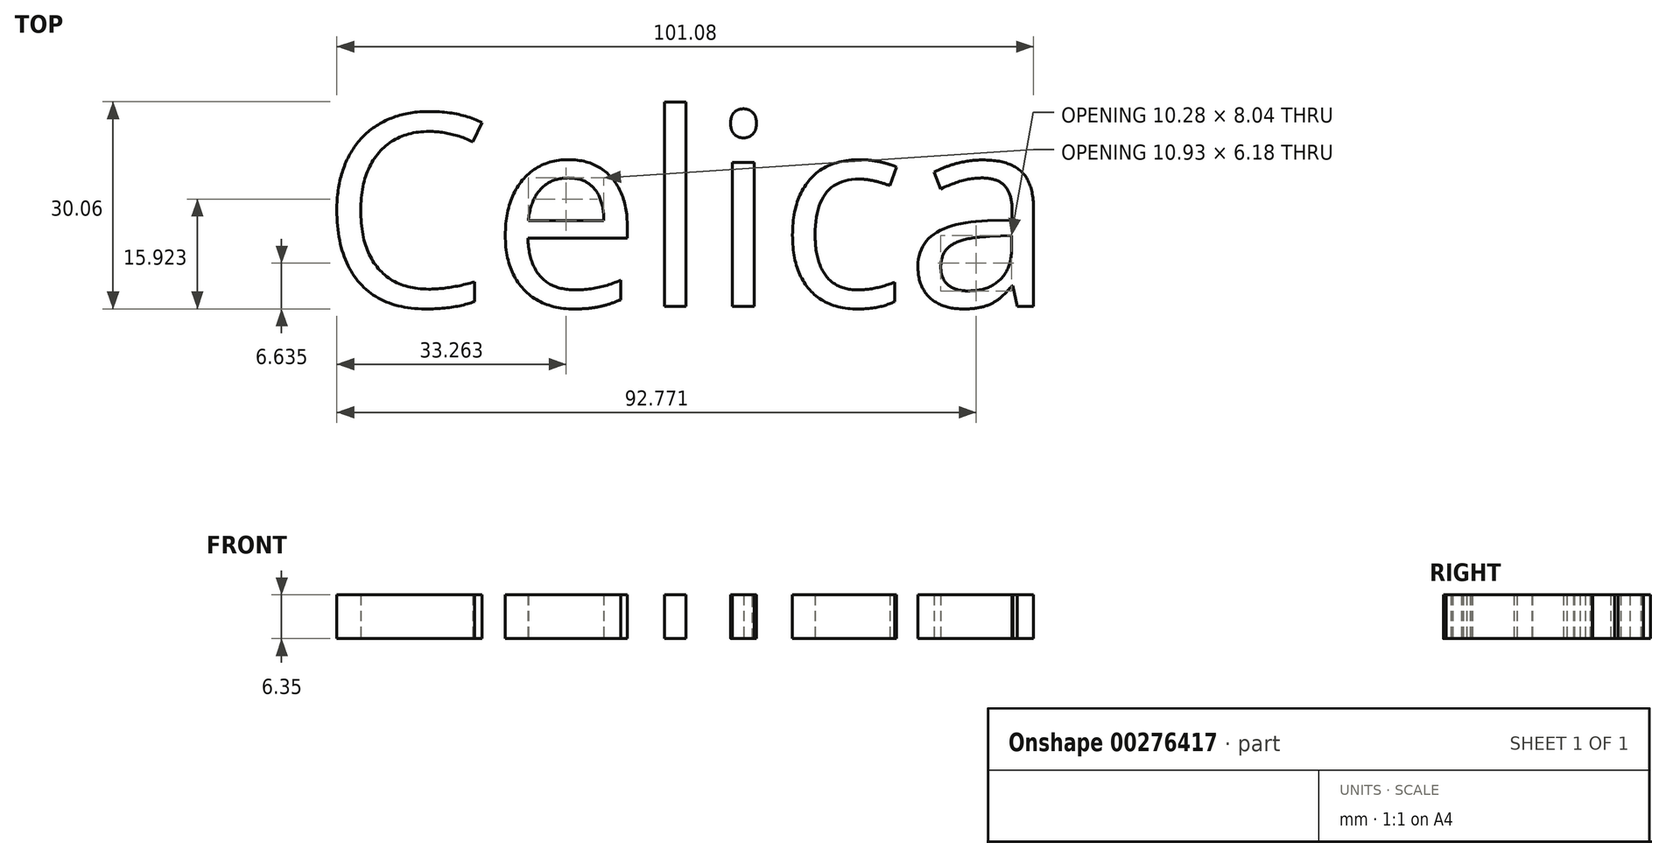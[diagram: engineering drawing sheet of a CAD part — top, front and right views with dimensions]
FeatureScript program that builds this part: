
annotation { "Feature Type Name" : "Feature", "Feature Type Description" : "" }
export const myFeature = defineFeature(function(context is Context, id is Id, definition is map)
    precondition{}
    {
        {
            var Q0;
            Q0=qCreatedBy(makeId("Top.planeOp"),FACE);
            var sketch = newSketch(context, id + "F0", { "sketchPlane" : qUnion([Q0])});
            skText(sketch, "E0", { "text": "Celica", "fontName": "OpenSans-Regular.ttf"});
            const initialGuessF0  = {"E0": [-0.053, 0, 1, 0, 0.02812]};
            skSetInitialGuess(sketch, initialGuessF0);
            skSolve(sketch);
        }
        {
            var Q0;
            Q0 = qSketchRegion(id + "F0", true);
            extrude(context, id + "F1", {"entities" : qUnion([Q0]), "depth" : 6.35 * mm});
        }
    });
